# Revit family: Lighting - Luminii - Hera
name_source: partatom
category: Lighting Fixtures
units: mm (PartAtom-declared; Revit-internal decimal feet)

## family parameters
Cut with Voids When Loaded = No
Host = Face
Light Source = Yes
OmniClass Number = 23.80.70.11.14.21
OmniClass Title = Spots and Tracklight Specialties
Part Type = Normal
Room Calculation Point = No
Round Connector Dimension = Use Diameter
Shared = Yes

## types (4) — shared parameters
Assembly Code = D5020230
Bottom Cap Material = Metal - Luminii - Silver Anodized Aluminum
CCT = 3000K
Color Filter = 16777215
Current Amps = 50 A
Default Elevation = 0"
Description = Acrylic globe pendant
Dimming Lamp Color Temperature Shift = <None>
Environment = Indoor
Finish = Metal - Luminii - Silver Anodized Aluminum
Frequency = 60 Hz
Has Battery Backup = No
Has Dimming = Yes
Housing Protection Rating = Consult Manufacturer Website for more Information
Initial Color Comments = Perfomance based on 3500K Photometric Web File
Instruction Sheet Link = https://www.luminii.com
Keynote = 26 50 00
Lamp = LED
Lamp Life = 1
Lens Material = Plastic - Luminii - Frosted Lens
Load Classification = Lighting
Manufacturer = Luminii
Mounting Method = Surface Mount
Number of Poles = 1
Operating Temperature = Consult Manufacturer Website for more Information
Phase = 1
Power Factor = 1
Power Source Type = Driver
Product Documentation Link = https://www.luminii.com
Product Name = Hera
Product Page URL = https://www.luminii.com
Tilt Angle = -90.00°
URL = https://www.luminii.com
Version = 2020 - v1.0a
Voltage = 120 V
Voltage Comments = 120V | 277V | 347V
Warranty URL = https://www.luminii.com

## per-type parameters (varying)
| type | Apparent Load | C Light Source Offset | Constraint | Depth | Lumen Output | Model | Photometric Web File | Wattage Comments | Width |
| Hera - 10" | 9 VA | 5" | 1 | 10" | 716 lm | 710 | 710-A90-35-07.ies | 9.1 W | 10" |
| Hera - 12" | 9 VA | 6" | 2 | 12" | 716 lm | 712 | 712-A90-35-07.ies | 9.1 | 12" |
| Hera - 16" | 8 VA | 8" | 3 | 16" | 684 lm | 716 | 716-A90-35-07.ies | 8.2 W | 16" |
| Hera - 20" | 8 VA | 10" | 4 | 20" | 698 lm | 720 | 720-A90-35-07.ies | 8.2 W | 20" |

## geometry (parser evidence)
native form markers: Sweep x8
no freeform markers — native parametric forms only
